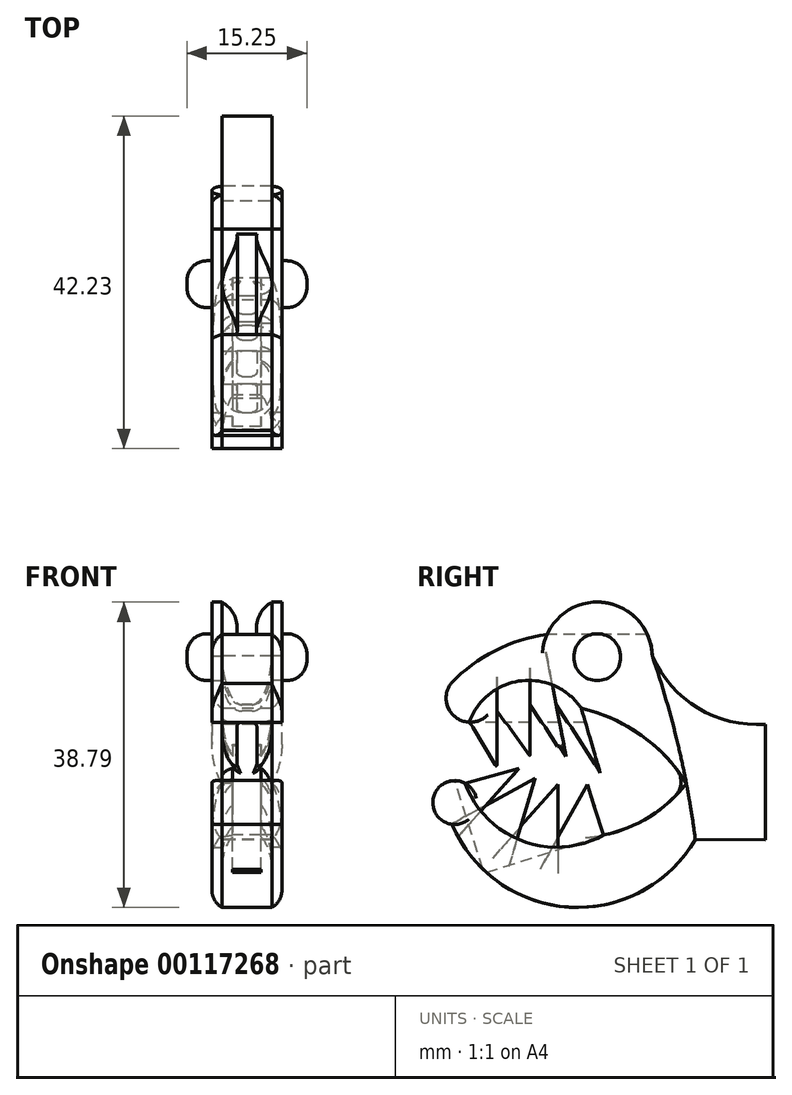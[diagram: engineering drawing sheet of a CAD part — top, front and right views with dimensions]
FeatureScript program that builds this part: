
annotation { "Feature Type Name" : "Feature", "Feature Type Description" : "" }
export const myFeature = defineFeature(function(context is Context, id is Id, definition is map)
    precondition{}
    {
        {
            var Q0;
            Q0=qCreatedBy(makeId("Right.planeOp"),FACE);
            var sketch = newSketch(context, id + "F0", { "sketchPlane" : qUnion([Q0])});
            skArc(sketch, "E0", {"start": v(21.56, -9.47) * mm, "mid": v(-3, 9.02) * mm, "end": v(-33.61, 6.04) * mm});
            skArc(sketch, "E1", {"start": v(-34.63, -9.47) * mm, "mid": v(-6.54, -23.36) * mm, "end": v(21.56, -9.47) * mm});
            skArc(sketch, "E2", {"start": v(-38.19, 15.95) * mm, "mid": v(-38.9, 9.6) * mm, "end": v(-33.61, 6.04) * mm});
            skArc(sketch, "E3", {"start": v(-13.84, 28.3) * mm, "mid": v(-27.06, 24.2) * mm, "end": v(-38.19, 15.95) * mm});
            skArc(sketch, "E4", {"start": v(-34.63, -9.47) * mm, "mid": v(-42.57, -12.7) * mm, "end": v(-37.93, -19.9) * mm});
            skArc(sketch, "E5", {"start": v(-37.93, -19.9) * mm, "mid": v(-8.23, -40.95) * mm, "end": v(23.85, -23.71) * mm});
            skArc(sketch, "E6", {"start": v(12.91, 22.82) * mm, "mid": v(1.74, 36.28) * mm, "end": v(-13.84, 28.3) * mm});
            skArc(sketch, "E7", {"start": v(12.91, 22.82) * mm, "mid": v(24.55, 9.64) * mm, "end": v(41.64, 5.53) * mm});
            skLineSegment(sketch, "E8", {"start": v(23.85, -23.71) * mm, "end": v(41.64, -23.92) * mm});
            skLineSegment(sketch, "E9", {"start": v(41.64, -23.92) * mm, "end": v(41.64, 5.53) * mm});
            skLineSegment(sketch, "E10", {"start": v(-33.61, 6.04) * mm, "end": v(-26.5, -5.91) * mm});
            skLineSegment(sketch, "E11", {"start": v(-26.5, -5.91) * mm, "end": v(-26.5, 8.86) * mm});
            skLineSegment(sketch, "E12", {"start": v(-26.5, 8.86) * mm, "end": v(-18.1, -2.86) * mm});
            skLineSegment(sketch, "E13", {"start": v(-18.1, -2.86) * mm, "end": v(-18.1, 10.45) * mm});
            skLineSegment(sketch, "E14", {"start": v(-18.1, 10.45) * mm, "end": v(-8.7, -4.13) * mm});
            skLineSegment(sketch, "E15", {"start": v(-8.7, -4.13) * mm, "end": v(-11.53, 10.5) * mm});
            skLineSegment(sketch, "E16", {"start": v(-11.53, 10.5) * mm, "end": v(-0.3, -6.93) * mm});
            skLineSegment(sketch, "E17", {"start": v(-0.3, -6.93) * mm, "end": v(-5.1, 9.55) * mm});
            skLineSegment(sketch, "E18", {"start": v(-34.63, -9.47) * mm, "end": v(-20.9, -5.66) * mm});
            skLineSegment(sketch, "E19", {"start": v(-20.9, -5.66) * mm, "end": v(-29.32, -15.04) * mm});
            skLineSegment(sketch, "E20", {"start": v(-29.32, -15.04) * mm, "end": v(-16.83, -8.2) * mm});
            skLineSegment(sketch, "E21", {"start": v(-16.83, -8.2) * mm, "end": v(-20.51, -20.48) * mm});
            skLineSegment(sketch, "E22", {"start": v(-20.51, -20.48) * mm, "end": v(-10.98, -9.73) * mm});
            skLineSegment(sketch, "E23", {"start": v(-10.98, -9.73) * mm, "end": v(-10.98, -23.07) * mm});
            skLineSegment(sketch, "E24", {"start": v(-10.98, -23.07) * mm, "end": v(-3.61, -9.73) * mm});
            skLineSegment(sketch, "E25", {"start": v(-3.61, -9.73) * mm, "end": v(0.5, -22.65) * mm});
            skSolve(sketch);
        }
        {
            var Q0;
            {var subQ8=sQuery(id+"F0.wireOp",EDGE,"E2");Q0=makeQuery(id+"F0.imprint","IMPRINT",FACE,{"disambiguationData":[TD([[makeQuery(id+"F0.imprint","IMPRINT",EDGE,{"derivedFrom":subQ8}),1.0]])]});}
            extrude(context, id + "F1", {"entities" : qUnion([Q0]), "depth" : 6.35 * mm, "hasSecondDirection" : true, "secondDirectionOppositeDirection" : true, "secondDirectionDepth" : 6.35 * mm});
        }
        {
            var Q0;
            {var subQ0=sQuery(id+"F0.wireOp",EDGE,"E24");Q0=makeQuery(id+"F0.imprint","IMPRINT",FACE,{"disambiguationData":[TD([[makeQuery(id+"F0.imprint","IMPRINT",EDGE,{"derivedFrom":subQ0}),-1.0]])]});}
            var Q1;
            {var subQ0=sQuery(id+"F0.wireOp",EDGE,"E16");Q1=makeQuery(id+"F0.imprint","IMPRINT",FACE,{"disambiguationData":[TD([[makeQuery(id+"F0.imprint","IMPRINT",EDGE,{"derivedFrom":subQ0}),1.0]])]});}
            var Q2;
            {var subQ0=sQuery(id+"F0.wireOp",EDGE,"E14");Q2=makeQuery(id+"F0.imprint","IMPRINT",FACE,{"disambiguationData":[TD([[makeQuery(id+"F0.imprint","IMPRINT",EDGE,{"derivedFrom":subQ0}),1.0]])]});}
            var Q3;
            {var subQ0=sQuery(id+"F0.wireOp",EDGE,"E12");Q3=makeQuery(id+"F0.imprint","IMPRINT",FACE,{"disambiguationData":[TD([[makeQuery(id+"F0.imprint","IMPRINT",EDGE,{"derivedFrom":subQ0}),1.0]])]});}
            var Q4;
            {var subQ0=sQuery(id+"F0.wireOp",EDGE,"E10");Q4=makeQuery(id+"F0.imprint","IMPRINT",FACE,{"disambiguationData":[TD([[makeQuery(id+"F0.imprint","IMPRINT",EDGE,{"derivedFrom":subQ0}),1.0]])]});}
            var Q5;
            {var subQ0=sQuery(id+"F0.wireOp",EDGE,"E18");Q5=makeQuery(id+"F0.imprint","IMPRINT",FACE,{"disambiguationData":[TD([[makeQuery(id+"F0.imprint","IMPRINT",EDGE,{"derivedFrom":subQ0}),-1.0]])]});}
            var Q6;
            {var subQ0=sQuery(id+"F0.wireOp",EDGE,"E20");Q6=makeQuery(id+"F0.imprint","IMPRINT",FACE,{"disambiguationData":[TD([[makeQuery(id+"F0.imprint","IMPRINT",EDGE,{"derivedFrom":subQ0}),-1.0]])]});}
            var Q7;
            {var subQ0=sQuery(id+"F0.wireOp",EDGE,"E22");Q7=makeQuery(id+"F0.imprint","IMPRINT",FACE,{"disambiguationData":[TD([[makeQuery(id+"F0.imprint","IMPRINT",EDGE,{"derivedFrom":subQ0}),-1.0]])]});}
            extrude(context, id + "F2", {"entities" : qUnion([Q0, Q1, Q2, Q3, Q4, Q5, Q6, Q7]), "operationType" : NewBodyOperationType.ADD, "depth" : 6.35 * mm, "hasSecondDirection" : true, "secondDirectionOppositeDirection" : true, "secondDirectionDepth" : 6.35 * mm});
        }
        {
            var Q0;
            Q0=qCreatedBy(makeId("Front.planeOp"),FACE);
            cPlane(context, id + "F3", {"entities" : qUnion([Q0]), "cplaneType" : CPlaneType.OFFSET, "offset" : 44.45 * mm, "width" : 152.4 * mm, "height" : 152.4 * mm});
        }
        {
            var Q0;
            Q0=qCreatedBy(id+"F3.planeOp",FACE);
            var sketch = newSketch(context, id + "F4", { "sketchPlane" : qUnion([Q0])});
            skLineSegment(sketch, "E26.0", {"start": v(1.27, 6.04) * mm, "end": v(-1.27, 6.04) * mm});
            skPoint(sketch, "E27.0", {"position": v(0, 6.04) * mm});
            skPoint(sketch, "E28.0", {"position": v(0, -5.91) * mm});
            skLineSegment(sketch, "E29", {"start": v(0, 6.04) * mm, "end": v(0, -5.91) * mm, "construction": true});
            skLineSegment(sketch, "E30.0", {"start": v(-2.54, 4.77) * mm, "end": v(-2.54, -4.64) * mm});
            skLineSegment(sketch, "E31.MirrorCS", {"start": v(2.54, 4.77) * mm, "end": v(2.54, -4.64) * mm});
            skPoint(sketch, "E32.newPointA", {"position": v(-6.35, 6.04) * mm});
            skPoint(sketch, "E32.newPointB", {"position": v(-2.54, 6.04) * mm});
            skArc(sketch, "E32.filletArc", {"start": v(-1.27, 6.04) * mm, "mid": v(-2.17, 5.66) * mm, "end": v(-2.54, 4.77) * mm});
            skPoint(sketch, "E33.newPointA", {"position": v(-2.54, -5.91) * mm});
            skPoint(sketch, "E33.newPointB", {"position": v(-6.35, -5.91) * mm});
            skPoint(sketch, "E34.newPointA", {"position": v(2.54, -5.91) * mm});
            skPoint(sketch, "E34.newPointB", {"position": v(6.35, -5.91) * mm});
            skPoint(sketch, "E35.newPointA", {"position": v(6.35, 6.04) * mm});
            skPoint(sketch, "E35.newPointB", {"position": v(2.54, 6.04) * mm});
            skArc(sketch, "E35.filletArc", {"start": v(2.54, 4.77) * mm, "mid": v(2.17, 5.66) * mm, "end": v(1.27, 6.04) * mm});
            skLineSegment(sketch, "E36.0", {"start": v(1.27, -7.66) * mm, "end": v(-1.27, -7.66) * mm});
            skLineSegment(sketch, "E37", {"start": v(1.27, -7.66) * mm, "end": v(2.54, -4.64) * mm});
            skLineSegment(sketch, "E38", {"start": v(-1.27, -7.66) * mm, "end": v(-2.54, -4.64) * mm});
            skSolve(sketch);
        }
        {
            var Q0;
            Q0=makeQuery(id+"F4.imprint","IMPRINT",FACE,{"disambiguationData":[TD([[makeQuery(id+"F4.imprint","IMPRINT",EDGE,{"derivedFrom":sQuery(id+"F4.wireOp",EDGE,"E26.0")}),1.0]])]});
            extrude(context, id + "F5", {"entities" : qUnion([Q0]), "operationType" : NewBodyOperationType.REMOVE, "oppositeDirection" : true, "depth" : 48.26 * mm});
        }
        {
            var Q0;
            Q0=makeQuery(id+"F2.opExtrude","SWEPT_FACE",FACE,{"disambiguationData":[OSD([sQuery(id+"F0.wireOp",EDGE,"E25")])]});
            var sketch = newSketch(context, id + "F6", { "sketchPlane" : qUnion([Q0])});
            skLineSegment(sketch, "E39.left", {"start": v(0, -21.74) * mm, "end": v(0, -8.18) * mm, "construction": true});
            skLineSegment(sketch, "E39.right", {"start": v(3.62, -21.74) * mm, "end": v(3.62, -8.18) * mm});
            skLineSegment(sketch, "E40.MirrorCS", {"start": v(-3.62, -21.74) * mm, "end": v(-3.62, -8.18) * mm});
            skLineSegment(sketch, "E41", {"start": v(3.62, -21.74) * mm, "end": v(-3.62, -21.74) * mm});
            skLineSegment(sketch, "E42.0", {"start": v(-3.62, 3.3) * mm, "end": v(3.62, 3.3) * mm});
            skLineSegment(sketch, "E43", {"start": v(-3.62, 3.3) * mm, "end": v(-3.62, -8.18) * mm});
            skLineSegment(sketch, "E44", {"start": v(3.62, 3.3) * mm, "end": v(3.62, -8.18) * mm});
            skSolve(sketch);
        }
        {
            var Q0;
            Q0=makeQuery(id+"F6.imprint","IMPRINT",FACE,{"disambiguationData":[TD([[makeQuery(id+"F6.imprint","IMPRINT",EDGE,{"derivedFrom":sQuery(id+"F6.wireOp",EDGE,"E39.right")}),1.0]])]});
            var Q1;
            Q1=makeQuery(id+"F6.imprint","IMPRINT",FACE,{"disambiguationData":[TD([[makeQuery(id+"F6.imprint","IMPRINT",EDGE,{"derivedFrom":sQuery(id+"F6.wireOp",EDGE,"E42.0")}),-1.0]])]});
            extrude(context, id + "F7", {"entities" : qUnion([Q0, Q1]), "operationType" : NewBodyOperationType.REMOVE, "oppositeDirection" : true, "depth" : 31.75 * mm});
        }
        {
            var Q0;
            {var subQ0=sQuery(id+"F0.wireOp",EDGE,"E1");var subQ1=sQuery(id+"F0.wireOp",EDGE,"E0");Q0=makeQuery(id+"F2.boolean.opBoolean","MERGE",FACE,{"derivedFrom":[makeQuery(id+"F1.opExtrude","CAP_FACE",FACE,{"disambiguationData":[OSD([subQ1,subQ0,sQuery(id+"F0.wireOp",EDGE,"E2"),sQuery(id+"F0.wireOp",EDGE,"E3"),sQuery(id+"F0.wireOp",EDGE,"E4"),sQuery(id+"F0.wireOp",EDGE,"E5"),sQuery(id+"F0.wireOp",EDGE,"E6"),sQuery(id+"F0.wireOp",EDGE,"E7"),sQuery(id+"F0.wireOp",EDGE,"E8"),sQuery(id+"F0.wireOp",EDGE,"E9")])],"isStart":false}),makeQuery(id+"F2.opExtrude","CAP_FACE",FACE,{"disambiguationData":[OSD([subQ1,sQuery(id+"F0.wireOp",EDGE,"E16"),sQuery(id+"F0.wireOp",EDGE,"E17")])],"isStart":false}),makeQuery(id+"F2.opExtrude","CAP_FACE",FACE,{"disambiguationData":[OSD([subQ1,sQuery(id+"F0.wireOp",EDGE,"E14"),sQuery(id+"F0.wireOp",EDGE,"E15")])],"isStart":false}),makeQuery(id+"F2.opExtrude","CAP_FACE",FACE,{"disambiguationData":[OSD([subQ1,sQuery(id+"F0.wireOp",EDGE,"E12"),sQuery(id+"F0.wireOp",EDGE,"E13")])],"isStart":false}),makeQuery(id+"F2.opExtrude","CAP_FACE",FACE,{"disambiguationData":[OSD([subQ1,sQuery(id+"F0.wireOp",EDGE,"E10"),sQuery(id+"F0.wireOp",EDGE,"E11")])],"isStart":false}),makeQuery(id+"F2.opExtrude","CAP_FACE",FACE,{"disambiguationData":[OSD([subQ0,sQuery(id+"F0.wireOp",EDGE,"E18"),sQuery(id+"F0.wireOp",EDGE,"E19")])],"isStart":false}),makeQuery(id+"F2.opExtrude","CAP_FACE",FACE,{"disambiguationData":[OSD([subQ0,sQuery(id+"F0.wireOp",EDGE,"E20"),sQuery(id+"F0.wireOp",EDGE,"E21")])],"isStart":false}),makeQuery(id+"F2.opExtrude","CAP_FACE",FACE,{"disambiguationData":[OSD([subQ0,sQuery(id+"F0.wireOp",EDGE,"E22"),sQuery(id+"F0.wireOp",EDGE,"E23")])],"isStart":false}),makeQuery(id+"F2.opExtrude","CAP_FACE",FACE,{"disambiguationData":[OSD([subQ0,sQuery(id+"F0.wireOp",EDGE,"E24"),sQuery(id+"F0.wireOp",EDGE,"E25")])],"isStart":false})]});}
            var sketch = newSketch(context, id + "F8", { "sketchPlane" : qUnion([Q0])});
            skArc(sketch, "E45.0.0", {"start": v(-5.1, 9.55) * mm, "mid": v(10.14, 2.72) * mm, "end": v(21.56, -9.47) * mm});
            skArc(sketch, "E45.0.1", {"start": v(21.56, -9.47) * mm, "mid": v(12.22, -17.97) * mm, "end": v(0.5, -22.65) * mm});
            skArc(sketch, "E45.0.10", {"start": v(-34.63, -9.47) * mm, "mid": v(-42.57, -12.7) * mm, "end": v(-37.93, -19.9) * mm});
            skArc(sketch, "E45.0.11", {"start": v(-37.93, -19.9) * mm, "mid": v(-8.23, -40.95) * mm, "end": v(23.85, -23.71) * mm});
            skArc(sketch, "E45.0.15", {"start": v(12.91, 22.82) * mm, "mid": v(1.74, 36.28) * mm, "end": v(-13.84, 28.3) * mm});
            skArc(sketch, "E45.0.16", {"start": v(-13.84, 28.3) * mm, "mid": v(-27.06, 24.2) * mm, "end": v(-38.19, 15.95) * mm});
            skArc(sketch, "E45.0.17", {"start": v(-38.19, 15.95) * mm, "mid": v(-38.9, 9.6) * mm, "end": v(-33.61, 6.04) * mm});
            skArc(sketch, "E46", {"start": v(-5.1, 9.55) * mm, "mid": v(-20.43, 16.55) * mm, "end": v(-33.61, 6.04) * mm});
            skArc(sketch, "E47", {"start": v(-34.63, -9.47) * mm, "mid": v(-20.1, -24.13) * mm, "end": v(0.5, -22.65) * mm});
            skPoint(sketch, "E45.0.24.end.orphan", {"position": v(-0.3, -6.93) * mm});
            skPoint(sketch, "E45.0.23.end.orphan", {"position": v(-11.53, 10.5) * mm});
            skPoint(sketch, "E45.0.22.end.orphan", {"position": v(-8.7, -4.13) * mm});
            skPoint(sketch, "E45.0.21.end.orphan", {"position": v(-18.1, 10.45) * mm});
            skPoint(sketch, "E45.0.20.end.orphan", {"position": v(-18.1, -2.86) * mm});
            skPoint(sketch, "E45.0.19.end.orphan", {"position": v(-26.5, 8.86) * mm});
            skPoint(sketch, "E45.0.18.end.orphan", {"position": v(-26.5, -5.91) * mm});
            skPoint(sketch, "E45.0.8.end.orphan", {"position": v(-20.9, -5.66) * mm});
            skPoint(sketch, "E45.0.7.end.orphan", {"position": v(-29.32, -15.04) * mm});
            skPoint(sketch, "E45.0.4.end.orphan", {"position": v(-10.98, -9.73) * mm});
            skPoint(sketch, "E45.0.3.end.orphan", {"position": v(-10.98, -23.07) * mm});
            skPoint(sketch, "E45.0.2.end.orphan", {"position": v(-3.61, -9.73) * mm});
            skPoint(sketch, "E45.0.6.end.orphan", {"position": v(-16.83, -8.2) * mm});
            skPoint(sketch, "E45.0.6.start.orphan", {"position": v(-20.51, -20.48) * mm});
            skArc(sketch, "E48", {"start": v(23.85, -23.71) * mm, "mid": v(19.57, -0.17) * mm, "end": v(12.91, 22.82) * mm});
            skPoint(sketch, "E45.0.13.end.orphan", {"position": v(41.64, 5.53) * mm});
            skPoint(sketch, "E45.0.13.start.orphan", {"position": v(41.64, -23.92) * mm});
            skSolve(sketch);
        }
        {
            var Q0;
            {var subQ0=sQuery(id+"F8.wireOp",EDGE,"E45.0.1");Q0=makeQuery(id+"F8.imprint","IMPRINT",FACE,{"disambiguationData":[TD([[makeQuery(id+"F8.imprint","IMPRINT",EDGE,{"derivedFrom":subQ0}),-1.0]])]});}
            var Q1;
            {var subQ1=sQuery(id+"F8.wireOp",EDGE,"E45.0.0");Q1=makeQuery(id+"F8.imprint","IMPRINT",FACE,{"disambiguationData":[TD([[makeQuery(id+"F8.imprint","IMPRINT",EDGE,{"derivedFrom":subQ1}),-1.0]])]});}
            extrude(context, id + "F9", {"entities" : qUnion([Q0, Q1]), "depth" : 2.54 * mm});
        }
        {
            var Q0;
            Q0=makeQuery(id+"F9.opExtrude","SWEPT_BODY",BODY,{"disambiguationData":[OSD([sQuery(id+"F8.wireOp",EDGE,"E45.0.0"),sQuery(id+"F8.wireOp",EDGE,"E45.0.15"),sQuery(id+"F8.wireOp",EDGE,"E45.0.16"),sQuery(id+"F8.wireOp",EDGE,"E45.0.17"),sQuery(id+"F8.wireOp",EDGE,"E46"),sQuery(id+"F8.wireOp",EDGE,"E48")])]});
            var Q1;
            Q1=makeQuery(id+"F9.opExtrude","SWEPT_BODY",BODY,{"disambiguationData":[OSD([sQuery(id+"F8.wireOp",EDGE,"E45.0.1"),sQuery(id+"F8.wireOp",EDGE,"E45.0.10"),sQuery(id+"F8.wireOp",EDGE,"E45.0.11"),sQuery(id+"F8.wireOp",EDGE,"E47"),sQuery(id+"F8.wireOp",EDGE,"E48")])]});
            var Q2;
            Q2=qCreatedBy(makeId("Right.planeOp"),FACE);
            mirror(context, id + "F10", {"entities" : qUnion([Q0, Q1]), "mirrorPlane" : qUnion([Q2])});
        }
        {
            var Q0;
            Q0=makeQuery(id+"F2.opExtrude","CAP_EDGE",EDGE,{"disambiguationData":[OSD([sQuery(id+"F0.wireOp",EDGE,"E18")])],"isStart":false});
            var Q1;
            Q1=makeQuery(id+"F2.opExtrude","CAP_EDGE",EDGE,{"disambiguationData":[OSD([sQuery(id+"F0.wireOp",EDGE,"E20")])],"isStart":false});
            var Q2;
            Q2=makeQuery(id+"F2.opExtrude","CAP_EDGE",EDGE,{"disambiguationData":[OSD([sQuery(id+"F0.wireOp",EDGE,"E22")])],"isStart":false});
            var Q3;
            Q3=makeQuery(id+"F2.opExtrude","CAP_EDGE",EDGE,{"disambiguationData":[OSD([sQuery(id+"F0.wireOp",EDGE,"E24")])],"isStart":false});
            var Q4;
            Q4=makeQuery(id+"F2.opExtrude","CAP_EDGE",EDGE,{"disambiguationData":[OSD([sQuery(id+"F0.wireOp",EDGE,"E16")])],"isStart":false});
            var Q5;
            Q5=makeQuery(id+"F2.opExtrude","CAP_EDGE",EDGE,{"disambiguationData":[OSD([sQuery(id+"F0.wireOp",EDGE,"E14")])],"isStart":false});
            var Q6;
            Q6=makeQuery(id+"F2.opExtrude","CAP_EDGE",EDGE,{"disambiguationData":[OSD([sQuery(id+"F0.wireOp",EDGE,"E12")])],"isStart":false});
            var Q7;
            Q7=makeQuery(id+"F2.opExtrude","CAP_EDGE",EDGE,{"disambiguationData":[OSD([sQuery(id+"F0.wireOp",EDGE,"E10")])],"isStart":false});
            var Q8;
            Q8=makeQuery(id+"F2.opExtrude","CAP_EDGE",EDGE,{"disambiguationData":[OSD([sQuery(id+"F0.wireOp",EDGE,"E16")])],"isStart":true});
            var Q9;
            Q9=makeQuery(id+"F2.opExtrude","CAP_EDGE",EDGE,{"disambiguationData":[OSD([sQuery(id+"F0.wireOp",EDGE,"E14")])],"isStart":true});
            var Q10;
            Q10=makeQuery(id+"F2.opExtrude","CAP_EDGE",EDGE,{"disambiguationData":[OSD([sQuery(id+"F0.wireOp",EDGE,"E12")])],"isStart":true});
            var Q11;
            Q11=makeQuery(id+"F2.opExtrude","CAP_EDGE",EDGE,{"disambiguationData":[OSD([sQuery(id+"F0.wireOp",EDGE,"E10")])],"isStart":true});
            var Q12;
            Q12=makeQuery(id+"F2.opExtrude","CAP_EDGE",EDGE,{"disambiguationData":[OSD([sQuery(id+"F0.wireOp",EDGE,"E19")])],"isStart":true});
            var Q13;
            Q13=makeQuery(id+"F2.opExtrude","CAP_EDGE",EDGE,{"disambiguationData":[OSD([sQuery(id+"F0.wireOp",EDGE,"E21")])],"isStart":true});
            var Q14;
            Q14=makeQuery(id+"F2.opExtrude","CAP_EDGE",EDGE,{"disambiguationData":[OSD([sQuery(id+"F0.wireOp",EDGE,"E23")])],"isStart":true});
            var Q15;
            Q15=makeQuery(id+"F2.opExtrude","CAP_EDGE",EDGE,{"disambiguationData":[OSD([sQuery(id+"F0.wireOp",EDGE,"E25")])],"isStart":true});
            fillet(context, id + "F11", {"entities" : qUnion([Q0, Q1, Q2, Q3, Q4, Q5, Q6, Q7, Q8, Q9, Q10, Q11, Q12, Q13, Q14, Q15]), "radius" : 5.08 * mm, "tangentPropagation" : true, "allowEdgeOverflow" : false});
        }
        {
            var Q0;
            Q0=qCreatedBy(makeId("Front.planeOp"),FACE);
            var sketch = newSketch(context, id + "F12", { "sketchPlane" : qUnion([Q0])});
            skLineSegment(sketch, "E49", {"start": v(-6.35, 36.57) * mm, "end": v(6.35, 36.57) * mm});
            skLineSegment(sketch, "E50.0", {"start": v(2.6, 28.3) * mm, "end": v(-2.6, 28.3) * mm});
            skArc(sketch, "E51", {"start": v(-2.6, 28.3) * mm, "mid": v(-3.12, 33.05) * mm, "end": v(-6.35, 36.57) * mm});
            skLineSegment(sketch, "E52", {"start": v(0, 28.3) * mm, "end": v(0, 36.57) * mm, "construction": true});
            skPoint(sketch, "E53.orphan", {"position": v(-6.35, 28.3) * mm});
            skArc(sketch, "E54.MirrorCS", {"start": v(2.6, 28.3) * mm, "mid": v(3.12, 33.05) * mm, "end": v(6.35, 36.57) * mm});
            skPoint(sketch, "E55.start.orphan", {"position": v(6.35, 28.3) * mm});
            skSolve(sketch);
        }
        {
            var Q0;
            Q0 = qSketchRegion(id + "F12", true);
            extrude(context, id + "F13", {"entities" : qUnion([Q0]), "operationType" : NewBodyOperationType.REMOVE, "oppositeDirection" : true, "depth" : 25.4 * mm, "hasSecondDirection" : true, "secondDirectionOppositeDirection" : false, "secondDirectionDepth" : 25.4 * mm});
        }
        {
            var Q0;
            Q0=makeQuery(id+"F10.opPattern","COPY",EDGE,{"derivedFrom":makeQuery(id+"F9.opExtrude","CAP_EDGE",EDGE,{"disambiguationData":[OSD([sQuery(id+"F8.wireOp",EDGE,"E45.0.16")])],"isStart":false}),"instanceName":"1"});
            var Q1;
            Q1=makeQuery(id+"F9.opExtrude","CAP_EDGE",EDGE,{"disambiguationData":[OSD([sQuery(id+"F8.wireOp",EDGE,"E45.0.16")])],"isStart":false});
            var Q2;
            Q2=makeQuery(id+"F10.opPattern","COPY",EDGE,{"derivedFrom":makeQuery(id+"F9.opExtrude","CAP_EDGE",EDGE,{"disambiguationData":[OSD([sQuery(id+"F8.wireOp",EDGE,"E45.0.11")])],"isStart":false}),"instanceName":"1"});
            var Q3;
            Q3=makeQuery(id+"F9.opExtrude","CAP_EDGE",EDGE,{"disambiguationData":[OSD([sQuery(id+"F8.wireOp",EDGE,"E45.0.11")])],"isStart":false});
            var Q4;
            Q4=makeQuery(id+"F10.opPattern","COPY",EDGE,{"derivedFrom":makeQuery(id+"F9.opExtrude","CAP_EDGE",EDGE,{"disambiguationData":[OSD([sQuery(id+"F8.wireOp",EDGE,"E45.0.1")])],"isStart":false}),"instanceName":"1"});
            var Q5;
            Q5=makeQuery(id+"F9.opExtrude","CAP_EDGE",EDGE,{"disambiguationData":[OSD([sQuery(id+"F8.wireOp",EDGE,"E45.0.1")])],"isStart":false});
            var Q6;
            Q6=makeQuery(id+"F10.opPattern","COPY",EDGE,{"derivedFrom":makeQuery(id+"F9.opExtrude","CAP_EDGE",EDGE,{"disambiguationData":[OSD([sQuery(id+"F8.wireOp",EDGE,"E45.0.0")])],"isStart":false}),"instanceName":"1"});
            var Q7;
            Q7=makeQuery(id+"F9.opExtrude","CAP_EDGE",EDGE,{"disambiguationData":[OSD([sQuery(id+"F8.wireOp",EDGE,"E45.0.0")])],"isStart":false});
            fillet(context, id + "F14", {"entities" : qUnion([Q0, Q1, Q2, Q3, Q4, Q5, Q6, Q7]), "radius" : 5.08 * mm, "tangentPropagation" : true, "allowEdgeOverflow" : false});
        }
        {
            var Q0;
            Q0=makeQuery(id+"F1.opExtrude","SWEPT_EDGE",EDGE,{"disambiguationData":[OSD([sQuery(id+"F0.wireOp",EDGE,"E0"),sQuery(id+"F0.wireOp",EDGE,"E1")])]});
            fillet(context, id + "F15", {"entities" : qUnion([Q0]), "radius" : 5.08 * mm, "tangentPropagation" : true, "allowEdgeOverflow" : false});
        }
        {
            var Q0;
            Q0=makeQuery(id+"F10.opPattern","COPY",FACE,{"derivedFrom":makeQuery(id+"F9.opExtrude","CAP_FACE",FACE,{"disambiguationData":[OSD([sQuery(id+"F8.wireOp",EDGE,"E45.0.0"),sQuery(id+"F8.wireOp",EDGE,"E45.0.15"),sQuery(id+"F8.wireOp",EDGE,"E45.0.16"),sQuery(id+"F8.wireOp",EDGE,"E45.0.17"),sQuery(id+"F8.wireOp",EDGE,"E46"),sQuery(id+"F8.wireOp",EDGE,"E48")])],"isStart":false}),"instanceName":"1"});
            var sketch = newSketch(context, id + "F16", { "sketchPlane" : qUnion([Q0])});
            skCircle(sketch, "E56", {"center": v(1.07, 22.58) * mm, "radius": 5.95 * mm});
            skSolve(sketch);
        }
        {
            var Q0;
            Q0=makeQuery(id+"F16.imprint","IMPRINT",FACE,{"disambiguationData":[TD([[makeQuery(id+"F16.imprint","IMPRINT",EDGE,{"derivedFrom":sQuery(id+"F16.wireOp",EDGE,"E56")}),1.0]])]});
            extrude(context, id + "F17", {"entities" : qUnion([Q0]), "depth" : 6.35 * mm});
        }
        {
            var Q0;
            Q0=makeQuery(id+"F17.opExtrude","CAP_EDGE",EDGE,{"disambiguationData":[OSD([sQuery(id+"F16.wireOp",EDGE,"E56")])],"isStart":false});
            fillet(context, id + "F18", {"entities" : qUnion([Q0]), "radius" : 5.08 * mm, "tangentPropagation" : true, "allowEdgeOverflow" : false});
        }
        {
            var Q0;
            Q0=makeQuery(id+"F17.opExtrude","SWEPT_BODY",BODY,{"disambiguationData":[OSD([sQuery(id+"F16.wireOp",EDGE,"E56")])]});
            var Q1;
            Q1=qCreatedBy(makeId("Right.planeOp"),FACE);
            mirror(context, id + "F19", {"operationType" : NewBodyOperationType.ADD, "entities" : qUnion([Q0]), "mirrorPlane" : qUnion([Q1])});
        }
        {
            var Q0;
            Q0=makeQuery(id+"F1.opExtrude","SWEPT_BODY",BODY,{"disambiguationData":[OSD([sQuery(id+"F0.wireOp",EDGE,"E0"),sQuery(id+"F0.wireOp",EDGE,"E1"),sQuery(id+"F0.wireOp",EDGE,"E2"),sQuery(id+"F0.wireOp",EDGE,"E3"),sQuery(id+"F0.wireOp",EDGE,"E4"),sQuery(id+"F0.wireOp",EDGE,"E5"),sQuery(id+"F0.wireOp",EDGE,"E6"),sQuery(id+"F0.wireOp",EDGE,"E7"),sQuery(id+"F0.wireOp",EDGE,"E8"),sQuery(id+"F0.wireOp",EDGE,"E9")])]});
            var Q1;
            Q1=makeQuery(id+"F9.opExtrude","SWEPT_BODY",BODY,{"disambiguationData":[OSD([sQuery(id+"F8.wireOp",EDGE,"E45.0.0"),sQuery(id+"F8.wireOp",EDGE,"E45.0.15"),sQuery(id+"F8.wireOp",EDGE,"E45.0.16"),sQuery(id+"F8.wireOp",EDGE,"E45.0.17"),sQuery(id+"F8.wireOp",EDGE,"E46"),sQuery(id+"F8.wireOp",EDGE,"E48")])]});
            var Q2;
            Q2=makeQuery(id+"F9.opExtrude","SWEPT_BODY",BODY,{"disambiguationData":[OSD([sQuery(id+"F8.wireOp",EDGE,"E45.0.1"),sQuery(id+"F8.wireOp",EDGE,"E45.0.10"),sQuery(id+"F8.wireOp",EDGE,"E45.0.11"),sQuery(id+"F8.wireOp",EDGE,"E47"),sQuery(id+"F8.wireOp",EDGE,"E48")])]});
            var Q3;
            Q3=makeQuery(id+"F10.opPattern","COPY",BODY,{"derivedFrom":makeQuery(id+"F9.opExtrude","SWEPT_BODY",BODY,{"disambiguationData":[OSD([sQuery(id+"F8.wireOp",EDGE,"E45.0.0"),sQuery(id+"F8.wireOp",EDGE,"E45.0.15"),sQuery(id+"F8.wireOp",EDGE,"E45.0.16"),sQuery(id+"F8.wireOp",EDGE,"E45.0.17"),sQuery(id+"F8.wireOp",EDGE,"E46"),sQuery(id+"F8.wireOp",EDGE,"E48")])]}),"instanceName":"1"});
            var Q4;
            Q4=makeQuery(id+"F10.opPattern","COPY",BODY,{"derivedFrom":makeQuery(id+"F9.opExtrude","SWEPT_BODY",BODY,{"disambiguationData":[OSD([sQuery(id+"F8.wireOp",EDGE,"E45.0.1"),sQuery(id+"F8.wireOp",EDGE,"E45.0.10"),sQuery(id+"F8.wireOp",EDGE,"E45.0.11"),sQuery(id+"F8.wireOp",EDGE,"E47"),sQuery(id+"F8.wireOp",EDGE,"E48")])]}),"instanceName":"1"});
            var Q5;
            Q5=makeQuery(id+"F17.opExtrude","SWEPT_BODY",BODY,{"disambiguationData":[OSD([sQuery(id+"F16.wireOp",EDGE,"E56")])]});
            var Q6;
            Q6=makeQuery(id+"F1.opExtrude","CAP_VERTEX",VERTEX,{"disambiguationData":[OSD([sQuery(id+"F0.wireOp",EDGE,"E7"),sQuery(id+"F0.wireOp",EDGE,"E9")])],"isStart":true});
            var Q7;
            Q7=makeQuery(id+"F1.opExtrude","CAP_VERTEX",VERTEX,{"disambiguationData":[OSD([sQuery(id+"F0.wireOp",EDGE,"E7"),sQuery(id+"F0.wireOp",EDGE,"E9")])],"isStart":true});
            transform(context, id + "F20", {"entities" : qUnion([Q0, Q1, Q2, Q3, Q4, Q5]), "transformType" : TransformType.SCALE_UNIFORMLY, "scale" : .5, "scalePoint" : qUnion([Q7]), "makeCopy" : false});
        }
    });
